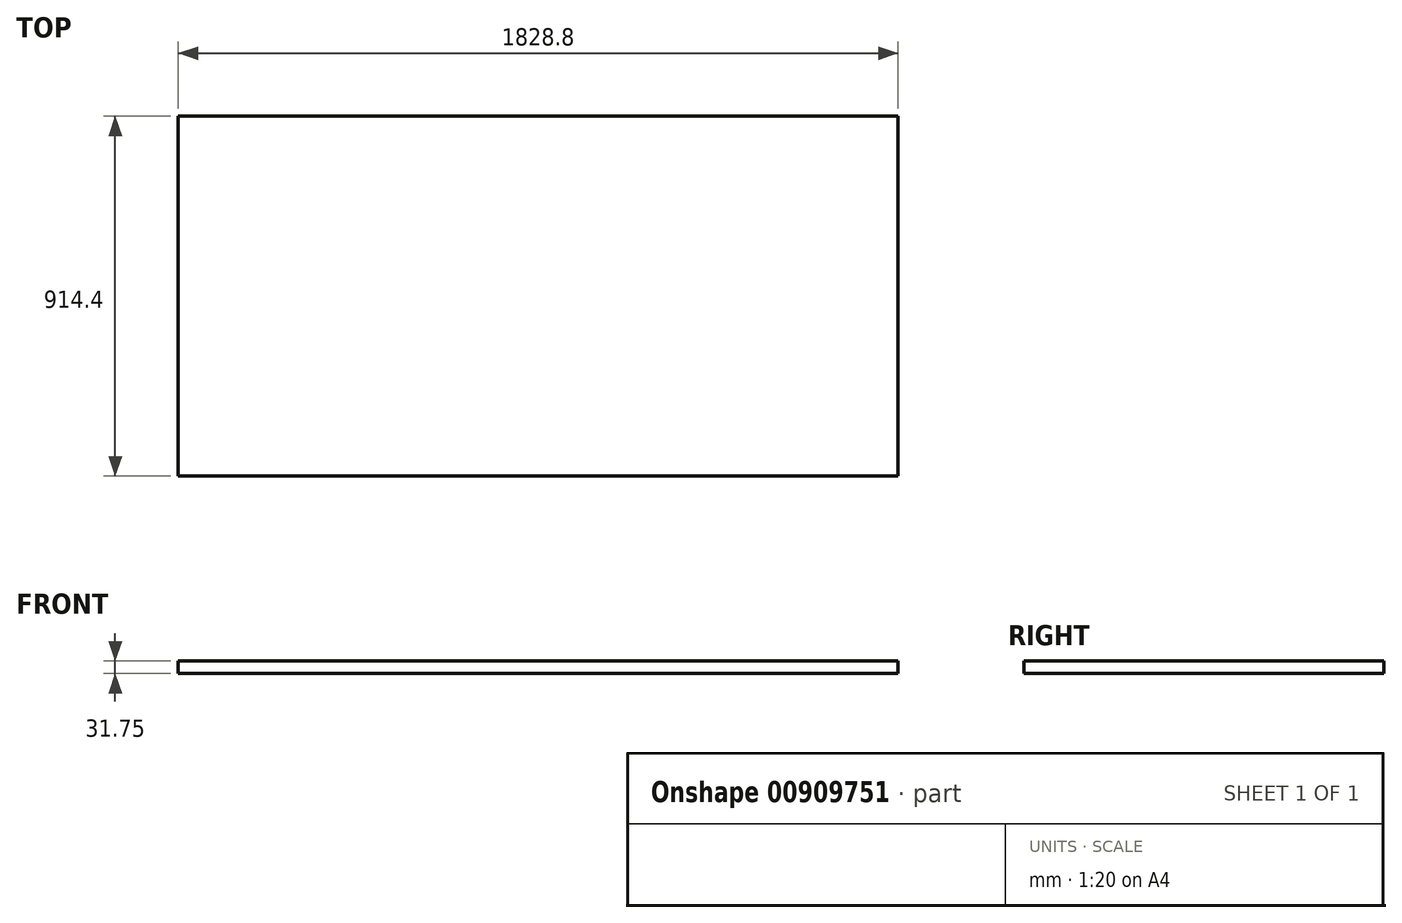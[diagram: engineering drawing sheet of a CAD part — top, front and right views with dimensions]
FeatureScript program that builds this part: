
annotation { "Feature Type Name" : "Feature", "Feature Type Description" : "" }
export const myFeature = defineFeature(function(context is Context, id is Id, definition is map)
    precondition{}
    {
        {
            var Q0;
            Q0=qCreatedBy(makeId("Top.planeOp"),FACE);
            var sketch = newSketch(context, id + "F0", { "sketchPlane" : qUnion([Q0])});
            skLineSegment(sketch, "E0.bottom", {"start": v(914.4, 457.2) * mm, "end": v(-914.4, 457.2) * mm});
            skLineSegment(sketch, "E0.top", {"start": v(914.4, -457.2) * mm, "end": v(-914.4, -457.2) * mm});
            skLineSegment(sketch, "E0.left", {"start": v(914.4, 457.2) * mm, "end": v(914.4, -457.2) * mm});
            skLineSegment(sketch, "E0.right", {"start": v(-914.4, 457.2) * mm, "end": v(-914.4, -457.2) * mm});
            skPoint(sketch, "E0.middle", {"position": v(0, 0) * mm});
            skSolve(sketch);
        }
        {
            var Q0;
            Q0=makeQuery(id+"F0.imprint","IMPRINT",FACE,{"disambiguationData":[TD([[makeQuery(id+"F0.imprint","IMPRINT",EDGE,{"derivedFrom":sQuery(id+"F0.wireOp",EDGE,"E0.bottom")}),1.0]])]});
            extrude(context, id + "F1", {"entities" : qUnion([Q0]), "depth" : 31.75 * mm, "offsetDistance" : 25.4 * mm});
        }
    });
